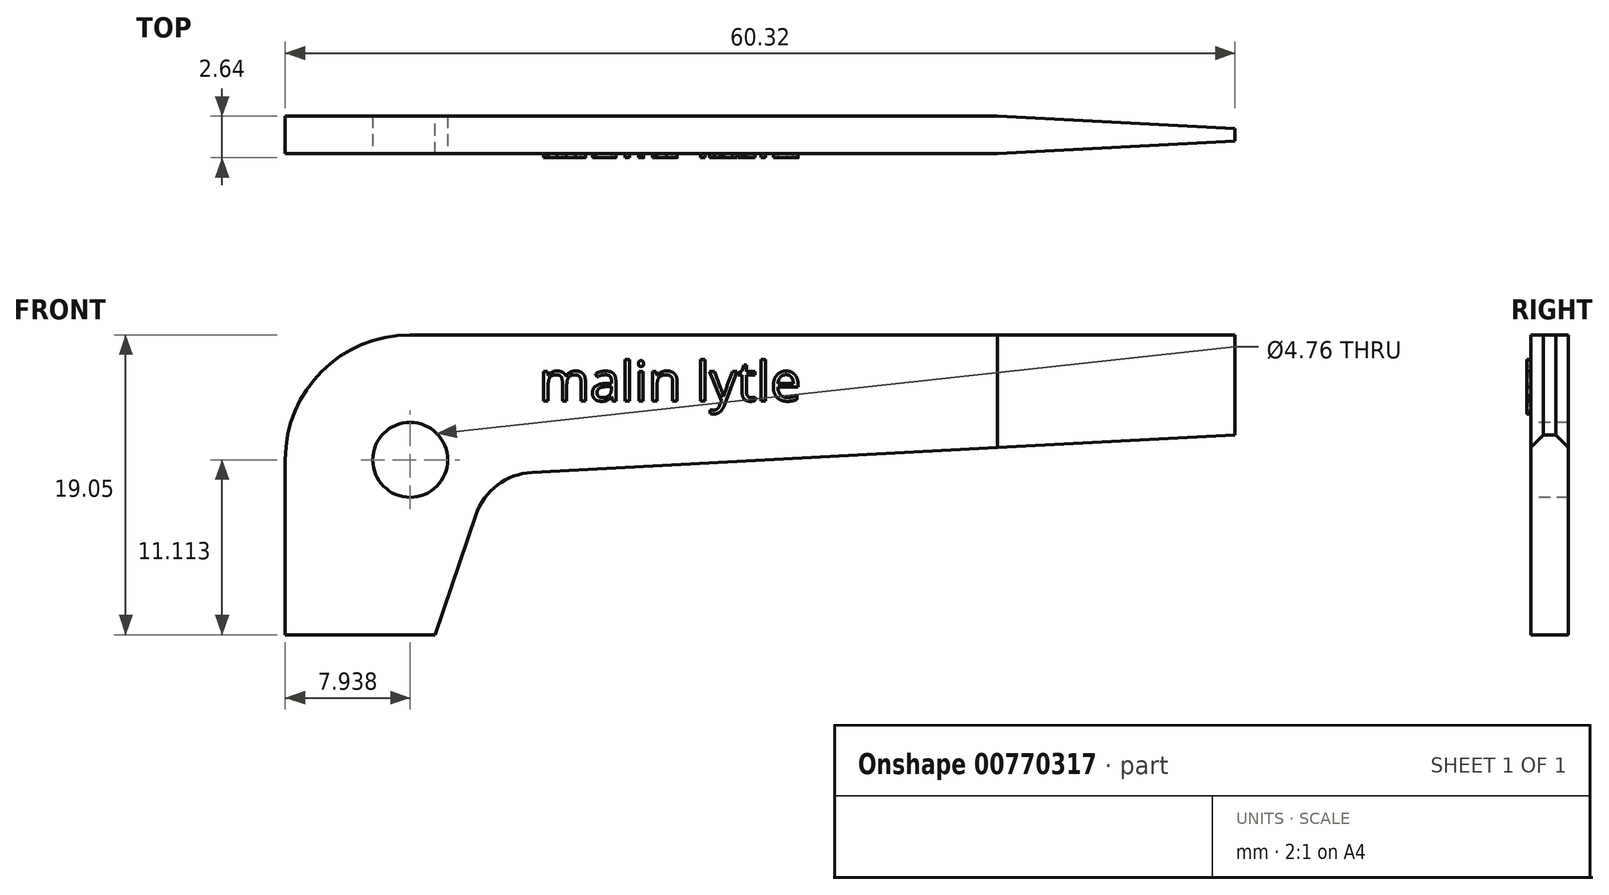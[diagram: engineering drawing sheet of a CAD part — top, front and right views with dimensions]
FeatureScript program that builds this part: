
annotation { "Feature Type Name" : "Feature", "Feature Type Description" : "" }
export const myFeature = defineFeature(function(context is Context, id is Id, definition is map)
    precondition{}
    {
        {
            var Q0;
            Q0=qCreatedBy(makeId("Front.planeOp"),FACE);
            var sketch = newSketch(context, id + "F0", { "sketchPlane" : qUnion([Q0])});
            skLineSegment(sketch, "E0.bottom", {"start": v(60.32, 19.05) * mm, "end": v(7.94, 19.05) * mm});
            skLineSegment(sketch, "E0.right", {"start": v(0, 11.11) * mm, "end": v(0, 0) * mm});
            skLineSegment(sketch, "E1", {"start": v(9.53, 0) * mm, "end": v(12.12, 7.63) * mm});
            skLineSegment(sketch, "E2", {"start": v(60.33, 12.7) * mm, "end": v(15.66, 10.31) * mm});
            skLineSegment(sketch, "E3", {"start": v(9.53, 0) * mm, "end": v(0, 0) * mm});
            skLineSegment(sketch, "E4", {"start": v(60.32, 19.05) * mm, "end": v(60.32, 12.7) * mm});
            skArc(sketch, "E5", {"start": v(15.66, 10.31) * mm, "mid": v(13.48, 9.51) * mm, "end": v(12.12, 7.63) * mm});
            skPoint(sketch, "E6.visualSharp", {"position": v(0, 19.05) * mm});
            skArc(sketch, "E6.filletArc", {"start": v(7.94, 19.05) * mm, "mid": v(2.32, 16.73) * mm, "end": v(0, 11.11) * mm});
            skSolve(sketch);
        }
        {
            var Q0;
            Q0=makeQuery(id+"F0.imprint","IMPRINT",FACE,{"disambiguationData":[TD([[makeQuery(id+"F0.imprint","IMPRINT",EDGE,{"derivedFrom":sQuery(id+"F0.wireOp",EDGE,"E0.bottom")}),1.0]])]});
            extrude(context, id + "F1", {"entities" : qUnion([Q0]), "depth" : 2.38 * mm, "offsetDistance" : 25.4 * mm});
        }
        {
            var Q0;
            Q0=makeQuery(id+"F1.opExtrude","CAP_FACE",FACE,{"disambiguationData":[OSD([sQuery(id+"F0.wireOp",EDGE,"E0.bottom"),sQuery(id+"F0.wireOp",EDGE,"E0.right"),sQuery(id+"F0.wireOp",EDGE,"E1"),sQuery(id+"F0.wireOp",EDGE,"E2"),sQuery(id+"F0.wireOp",EDGE,"E3"),sQuery(id+"F0.wireOp",EDGE,"E4"),sQuery(id+"F0.wireOp",EDGE,"E5"),sQuery(id+"F0.wireOp",EDGE,"E6.filletArc")])],"isStart":false});
            var sketch = newSketch(context, id + "F2", { "sketchPlane" : qUnion([Q0])});
            skCircle(sketch, "E7", {"center": v(7.94, 11.11) * mm, "radius": 2.38 * mm});
            skSolve(sketch);
        }
        {
            var Q0;
            Q0=makeQuery(id+"F2.imprint","IMPRINT",FACE,{"disambiguationData":[TD([[makeQuery(id+"F2.imprint","IMPRINT",EDGE,{"derivedFrom":sQuery(id+"F2.wireOp",EDGE,"E7")}),1.0]])]});
            extrude(context, id + "F3", {"entities" : qUnion([Q0]), "operationType" : NewBodyOperationType.REMOVE, "endBound" : BoundingType.THROUGH_ALL, "oppositeDirection" : true, "depth" : 25.4 * mm, "offsetDistance" : 25.4 * mm});
        }
        {
            var Q0;
            Q0=makeQuery(id+"F1.opExtrude","SWEPT_FACE",FACE,{"disambiguationData":[OSD([sQuery(id+"F0.wireOp",EDGE,"E0.bottom")])]});
            var sketch = newSketch(context, id + "F4", { "sketchPlane" : qUnion([Q0])});
            skLineSegment(sketch, "E8", {"start": v(60.32, -0.8) * mm, "end": v(45.24, 0) * mm});
            skLineSegment(sketch, "E9.MirrorCS", {"start": v(60.32, -1.59) * mm, "end": v(45.24, -2.38) * mm});
            skSolve(sketch);
        }
        {
            var Q0;
            {var subQ0=sQuery(id+"F4.wireOp",EDGE,"E9.MirrorCS");Q0=makeQuery(id+"F4.imprint","IMPRINT",FACE,{"disambiguationData":[TD([[makeQuery(id+"F4.imprint","IMPRINT",EDGE,{"derivedFrom":subQ0}),1.0]])]});}
            var Q1;
            {var subQ0=sQuery(id+"F4.wireOp",EDGE,"E8");Q1=makeQuery(id+"F4.imprint","IMPRINT",FACE,{"disambiguationData":[TD([[makeQuery(id+"F4.imprint","IMPRINT",EDGE,{"derivedFrom":subQ0}),-1.0]])]});}
            extrude(context, id + "F5", {"entities" : qUnion([Q0, Q1]), "operationType" : NewBodyOperationType.REMOVE, "oppositeDirection" : true, "depth" : 25.4 * mm, "offsetDistance" : 25.4 * mm});
        }
        {
            var Q0;
            Q0=makeQuery(id+"F1.opExtrude","CAP_FACE",FACE,{"disambiguationData":[OSD([sQuery(id+"F0.wireOp",EDGE,"E0.bottom"),sQuery(id+"F0.wireOp",EDGE,"E0.right"),sQuery(id+"F0.wireOp",EDGE,"E1"),sQuery(id+"F0.wireOp",EDGE,"E2"),sQuery(id+"F0.wireOp",EDGE,"E3"),sQuery(id+"F0.wireOp",EDGE,"E4"),sQuery(id+"F0.wireOp",EDGE,"E5"),sQuery(id+"F0.wireOp",EDGE,"E6.filletArc")])],"isStart":false});
            var sketch = newSketch(context, id + "F6", { "sketchPlane" : qUnion([Q0])});
            skText(sketch, "E10", { "text": "malin lytle", "fontName": "OpenSans-Regular.ttf"});
            const initialGuessF6  = {"E10": [0.01612, 0.01486, 1, 0, 0.0025]};
            skSetInitialGuess(sketch, initialGuessF6);
            skSolve(sketch);
        }
        {
            var Q0;
            Q0 = qSketchRegion(id + "F6", true);
            extrude(context, id + "F7", {"entities" : qUnion([Q0]), "operationType" : NewBodyOperationType.ADD, "depth" : 0.25 * mm, "offsetDistance" : 25.4 * mm});
        }
    });
